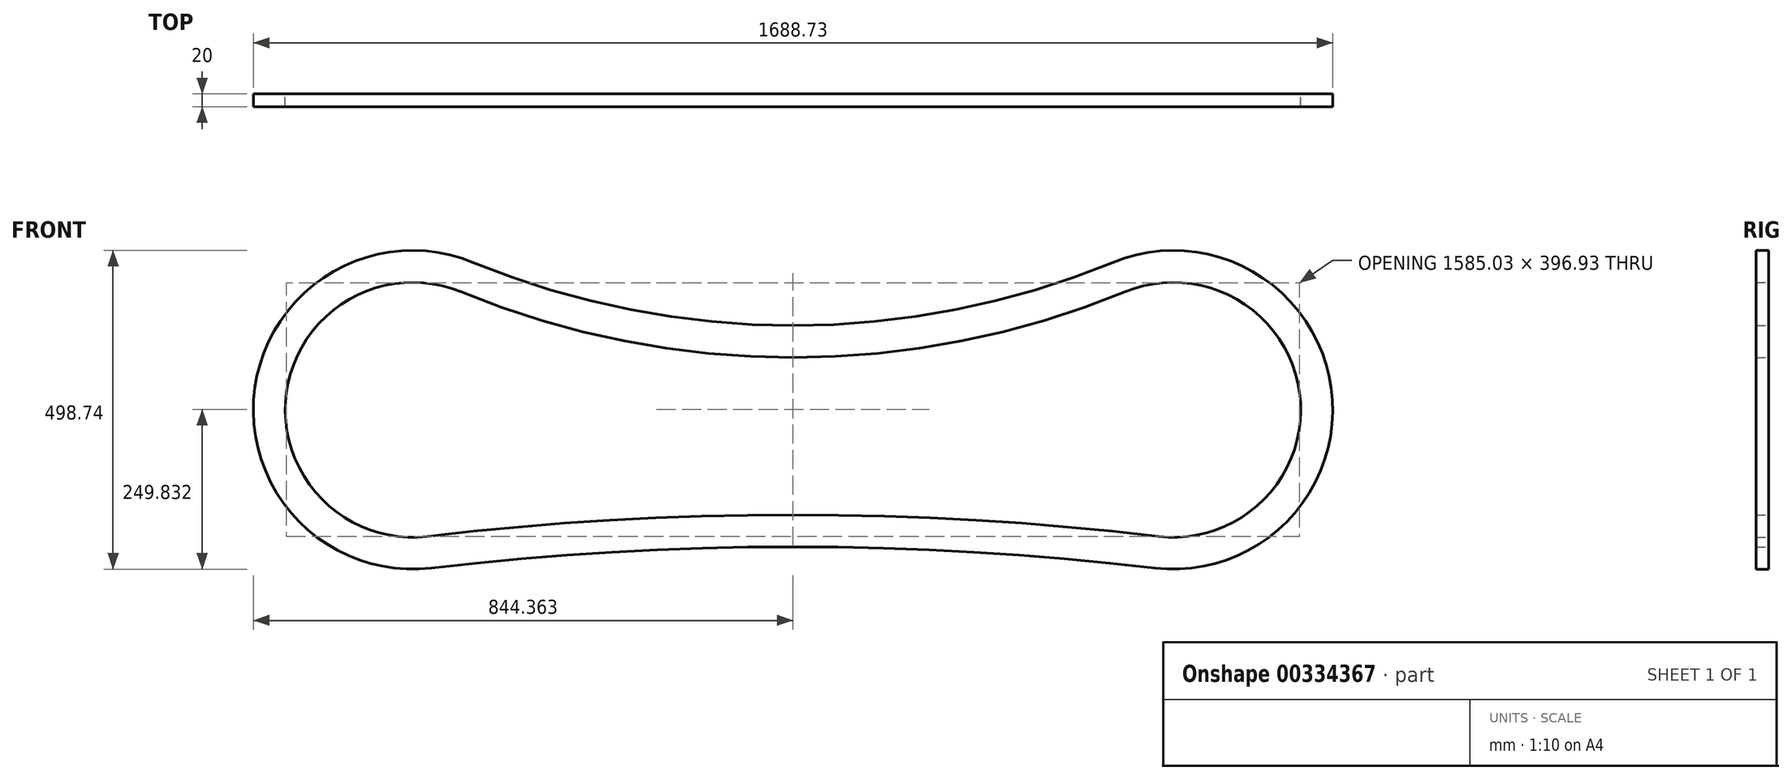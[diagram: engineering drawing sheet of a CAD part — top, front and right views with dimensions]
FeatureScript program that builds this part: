
annotation { "Feature Type Name" : "Feature", "Feature Type Description" : "" }
export const myFeature = defineFeature(function(context is Context, id is Id, definition is map)
    precondition{}
    {
        {
            var Q0;
            Q0=qCreatedBy(makeId("Front.planeOp"),FACE);
            var sketch = newSketch(context, id + "F0", { "sketchPlane" : qUnion([Q0])});
            skArc(sketch, "E0", {"start": v(-503.16, 216.76) * mm, "mid": v(-844.94, 19.98) * mm, "end": v(-568.8, -261.58) * mm});
            skArc(sketch, "E1", {"start": v(563.02, -261.58) * mm, "mid": v(839.17, 19.98) * mm, "end": v(497.39, 216.76) * mm});
            skLineSegment(sketch, "E2", {"start": v(-597.89, -13.92) * mm, "end": v(592.11, -13.92) * mm});
            skArc(sketch, "E3", {"start": v(563.02, -261.58) * mm, "mid": v(-2.89, -228.45) * mm, "end": v(-568.8, -261.58) * mm});
            skPoint(sketch, "E3.centerSnap0", {"position": v(-2.89, -13.92) * mm});
            skArc(sketch, "E4", {"start": v(-503.16, 216.76) * mm, "mid": v(-2.89, 118.04) * mm, "end": v(497.39, 216.76) * mm});
            skArc(sketch, "E5.0", {"start": v(-522.16, 170.5) * mm, "mid": v(-795.4, 13.18) * mm, "end": v(-574.62, -211.92) * mm});
            skArc(sketch, "E5.1", {"start": v(-522.16, 170.5) * mm, "mid": v(-2.89, 68.04) * mm, "end": v(516.38, 170.5) * mm});
            skArc(sketch, "E5.2", {"start": v(568.85, -211.92) * mm, "mid": v(789.63, 13.18) * mm, "end": v(516.38, 170.5) * mm});
            skArc(sketch, "E5.3", {"start": v(568.85, -211.92) * mm, "mid": v(-2.89, -178.45) * mm, "end": v(-574.62, -211.92) * mm});
            skSolve(sketch);
        }
        {
            var Q0;
            Q0=makeQuery(id+"F0.imprint","IMPRINT",FACE,{"disambiguationData":[TD([[makeQuery(id+"F0.imprint","IMPRINT",EDGE,{"derivedFrom":sQuery(id+"F0.wireOp",EDGE,"E0")}),1.0]])]});
            extrude(context, id + "F1", {"entities" : qUnion([Q0]), "depth" : 20 * mm});
        }
    });
